# Revit family: ЭВАН NEXT 18-28 кВт
name_source: partatom
category: Оборудование
units: mm (PartAtom-declared; Revit-internal decimal feet)

## family parameters
Всегда вертикально = Да
Классификация = Нет
На основе рабочей плоскости = Да
Общий = Нет
При загрузке вырезать с полостями = Нет
Размер круглого соединителя = Использовать диаметр
Тип детали = Нормальный
Точка расчета площади = Нет

## types (4) — shared parameters
ADSK_Классификация нагрузок = Прочее
ADSK_Количество фаз = 3
ADSK_Материал = Сталь
ADSK_Размер_Высота = 684 мм
ADSK_Размер_Длина = 275 мм
ADSK_Размер_Ширина = 185 мм
ADSK_Расход теплоносителя = 0.0 м³/ч
Dn = 32 мм
URL = https://www.evan.ru
База = ЭЛЕКТРИЧЕСКИЙ ТЕПЛОГЕНЕРАТОР (КОТЕЛ)
Диапазон регулируемых температур теплоносителя, оС = От +30 до +85
Максимальная температура теплоносителя, оС = +85
Материал корпуса = Сталь
Минимальная температура теплоносителя, оС = +30
Объем колбы котла, л = 7,5
Рабочее давление, МПа = 0,07-0,3
Резьба патрубков для подключения трубопроводов теплоносителя = G 1 1/4
zero-valued in all types: Отметка по умолчанию

## per-type parameters (varying)
| type | ADSK_Номинальная мощность | Потребляемая электрическая мощность при максимальной тепловой мощность  в час, кВт/ч |
| ЭВАН NEXT 18 кВт | 18000 Вт | 18.9 |
| ЭВАН NEXT 21 кВт | 21000 Вт | 22.05 |
| ЭВАН NEXT 24 кВт | 24000 Вт | 25.2 |
| ЭВАН NEXT 28 кВт | 28000 Вт | 29.4 |
